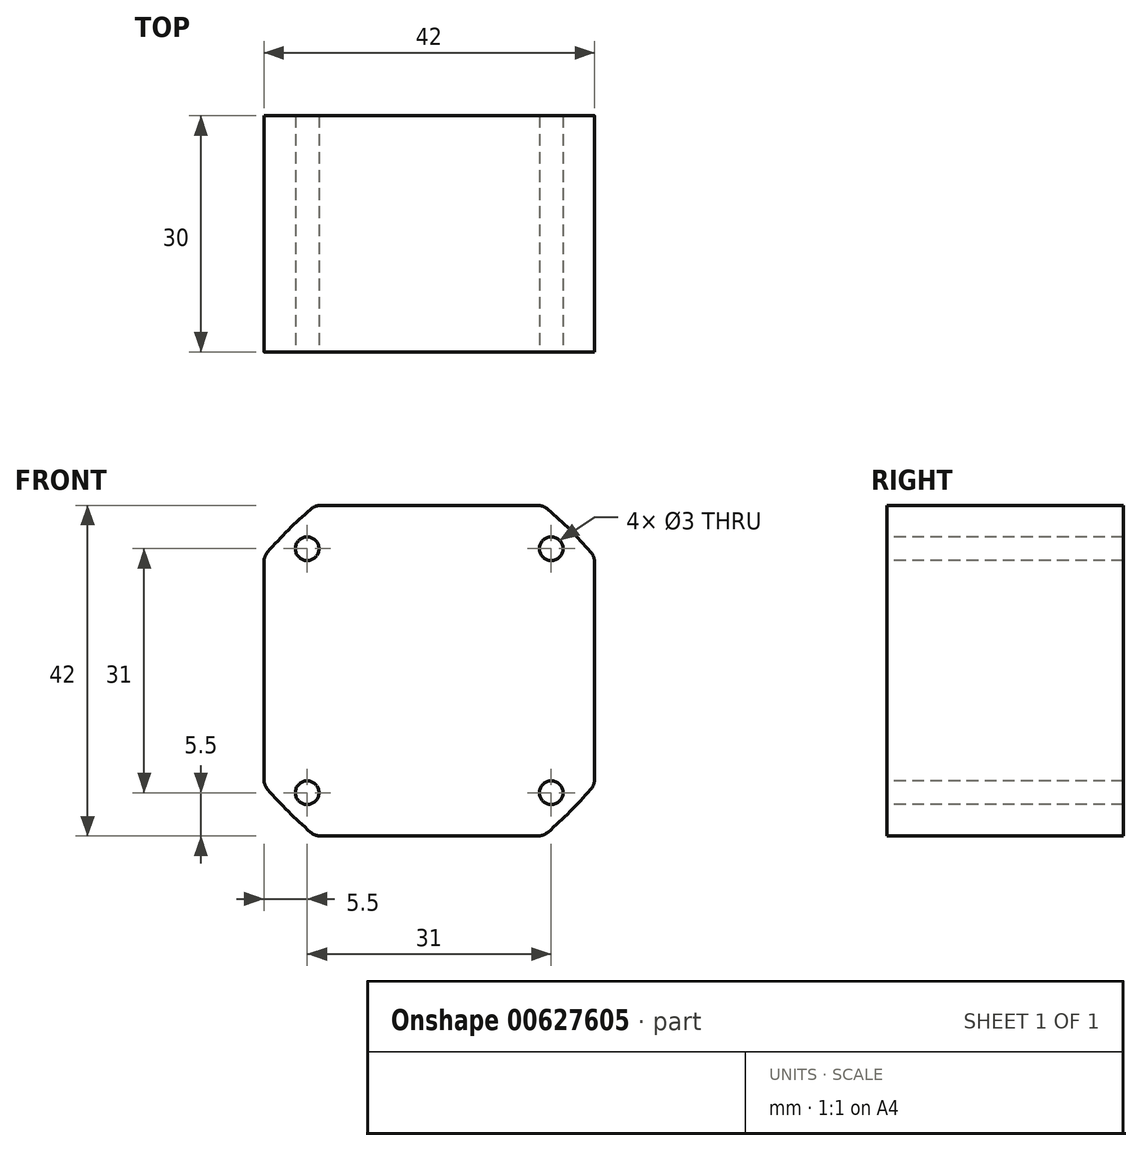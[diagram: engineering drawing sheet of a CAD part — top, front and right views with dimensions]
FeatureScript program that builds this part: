
annotation { "Feature Type Name" : "Feature", "Feature Type Description" : "" }
export const myFeature = defineFeature(function(context is Context, id is Id, definition is map)
    precondition{}
    {
        {
            var Q0;
            Q0=qCreatedBy(makeId("Front.planeOp"),FACE);
            var sketch = newSketch(context, id + "F0", { "sketchPlane" : qUnion([Q0])});
            skLineSegment(sketch, "E0.bottom", {"start": v(-21, 21) * mm, "end": v(21, 21) * mm, "construction": true});
            skLineSegment(sketch, "E0.top", {"start": v(-21, -21) * mm, "end": v(21, -21) * mm, "construction": true});
            skLineSegment(sketch, "E0.left", {"start": v(-21, 21) * mm, "end": v(-21, -21) * mm, "construction": true});
            skLineSegment(sketch, "E0.right", {"start": v(21, 21) * mm, "end": v(21, -21) * mm, "construction": true});
            skPoint(sketch, "E0.middle", {"position": v(0, 0) * mm});
            skArc(sketch, "E1", {"start": v(-21, 14.51) * mm, "mid": v(-17.9, 17.9) * mm, "end": v(-14.51, 21) * mm});
            skArc(sketch, "E2.1.0", {"start": v(-14.51, -21) * mm, "mid": v(-17.9, -17.9) * mm, "end": v(-21, -14.51) * mm});
            skArc(sketch, "E2.2.0", {"start": v(21, -14.51) * mm, "mid": v(17.9, -17.9) * mm, "end": v(14.51, -21) * mm});
            skArc(sketch, "E2.3.0", {"start": v(14.51, 21) * mm, "mid": v(17.9, 17.9) * mm, "end": v(21, 14.51) * mm});
            skLineSegment(sketch, "E3", {"start": v(-14.51, 21) * mm, "end": v(14.51, 21) * mm});
            skLineSegment(sketch, "E4", {"start": v(21, 14.51) * mm, "end": v(21, -14.51) * mm});
            skLineSegment(sketch, "E5", {"start": v(14.51, -21) * mm, "end": v(-14.51, -21) * mm});
            skLineSegment(sketch, "E6", {"start": v(-21, -14.51) * mm, "end": v(-21, 14.51) * mm});
            skSolve(sketch);
        }
        {
            var Q0;
            Q0 = qSketchRegion(id + "F0", true);
            extrude(context, id + "F1", {"entities" : qUnion([Q0]), "endBound" : BoundingType.SYMMETRIC, "depth" : 30 * mm, "offsetDistance" : 25 * mm});
        }
        {
            var Q0;
            Q0=makeQuery(id+"F1.opExtrude","SWEPT_EDGE",EDGE,{"disambiguationData":[OSD([sQuery(id+"F0.wireOp",EDGE,"E2.3.0"),sQuery(id+"F0.wireOp",EDGE,"E3")])]});
            var Q1;
            Q1=makeQuery(id+"F1.opExtrude","SWEPT_EDGE",EDGE,{"disambiguationData":[OSD([sQuery(id+"F0.wireOp",EDGE,"E2.3.0"),sQuery(id+"F0.wireOp",EDGE,"E4")])]});
            var Q2;
            Q2=makeQuery(id+"F1.opExtrude","SWEPT_EDGE",EDGE,{"disambiguationData":[OSD([sQuery(id+"F0.wireOp",EDGE,"E2.2.0"),sQuery(id+"F0.wireOp",EDGE,"E4")])]});
            var Q3;
            Q3=makeQuery(id+"F1.opExtrude","SWEPT_EDGE",EDGE,{"disambiguationData":[OSD([sQuery(id+"F0.wireOp",EDGE,"E2.2.0"),sQuery(id+"F0.wireOp",EDGE,"E5")])]});
            var Q4;
            Q4=makeQuery(id+"F1.opExtrude","SWEPT_EDGE",EDGE,{"disambiguationData":[OSD([sQuery(id+"F0.wireOp",EDGE,"E2.1.0"),sQuery(id+"F0.wireOp",EDGE,"E5")])]});
            var Q5;
            Q5=makeQuery(id+"F1.opExtrude","SWEPT_EDGE",EDGE,{"disambiguationData":[OSD([sQuery(id+"F0.wireOp",EDGE,"E2.1.0"),sQuery(id+"F0.wireOp",EDGE,"E6")])]});
            var Q6;
            Q6=makeQuery(id+"F1.opExtrude","SWEPT_EDGE",EDGE,{"disambiguationData":[OSD([sQuery(id+"F0.wireOp",EDGE,"E1"),sQuery(id+"F0.wireOp",EDGE,"E6")])]});
            var Q7;
            Q7=makeQuery(id+"F1.opExtrude","SWEPT_EDGE",EDGE,{"disambiguationData":[OSD([sQuery(id+"F0.wireOp",EDGE,"E1"),sQuery(id+"F0.wireOp",EDGE,"E3")])]});
            fillet(context, id + "F2", {"entities" : qUnion([Q0, Q1, Q2, Q3, Q4, Q5, Q6, Q7]), "radius" : 2 * mm, "tangentPropagation" : true, "allowEdgeOverflow" : false});
        }
        {
            var Q0;
            Q0=makeQuery(id+"F1.opExtrude","CAP_FACE",FACE,{"disambiguationData":[OSD([sQuery(id+"F0.wireOp",EDGE,"E1"),sQuery(id+"F0.wireOp",EDGE,"E2.1.0"),sQuery(id+"F0.wireOp",EDGE,"E2.2.0"),sQuery(id+"F0.wireOp",EDGE,"E2.3.0"),sQuery(id+"F0.wireOp",EDGE,"E3"),sQuery(id+"F0.wireOp",EDGE,"E4"),sQuery(id+"F0.wireOp",EDGE,"E5"),sQuery(id+"F0.wireOp",EDGE,"E6")])],"isStart":false});
            var sketch = newSketch(context, id + "F3", { "sketchPlane" : qUnion([Q0])});
            skCircle(sketch, "E7", {"center": v(15.5, 15.5) * mm, "radius": 1.5 * mm});
            skCircle(sketch, "E8.1.0", {"center": v(-15.5, 15.5) * mm, "radius": 1.5 * mm});
            skCircle(sketch, "E8.2.0", {"center": v(-15.5, -15.5) * mm, "radius": 1.5 * mm});
            skCircle(sketch, "E8.3.0", {"center": v(15.5, -15.5) * mm, "radius": 1.5 * mm});
            skPoint(sketch, "E8.center", {"position": v(0, 0) * mm});
            skSolve(sketch);
        }
        {
            var Q0;
            Q0 = qSketchRegion(id + "F3", true);
            extrude(context, id + "F4", {"entities" : qUnion([Q0]), "operationType" : NewBodyOperationType.REMOVE, "endBound" : BoundingType.THROUGH_ALL, "oppositeDirection" : true, "depth" : 25 * mm, "offsetDistance" : 25 * mm});
        }
    });
